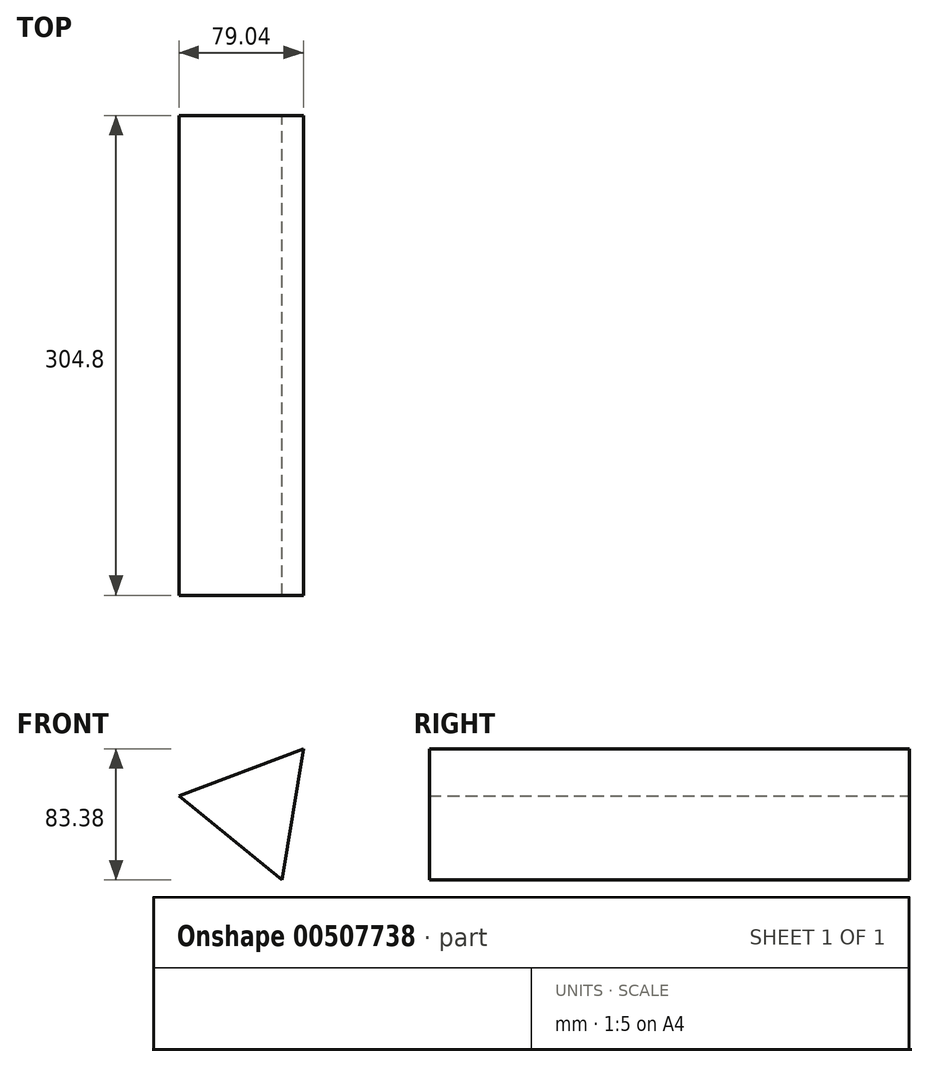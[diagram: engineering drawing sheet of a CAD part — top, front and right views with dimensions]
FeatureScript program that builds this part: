
annotation { "Feature Type Name" : "Feature", "Feature Type Description" : "" }
export const myFeature = defineFeature(function(context is Context, id is Id, definition is map)
    precondition{}
    {
        {
            var Q0;
            Q0=qCreatedBy(makeId("Front.planeOp"),FACE);
            var sketch = newSketch(context, id + "F0", { "sketchPlane" : qUnion([Q0])});
            skCircle(sketch, "E0.cCircle", {"center": v(0, 0) * mm, "radius": 48.78 * mm, "construction": true});
            skLineSegment(sketch, "E0.0", {"start": v(30.9, 37.75) * mm, "end": v(17.24, -45.63) * mm});
            skLineSegment(sketch, "E0.1", {"start": v(17.24, -45.63) * mm, "end": v(-48.14, 7.88) * mm});
            skLineSegment(sketch, "E0.2", {"start": v(-48.14, 7.88) * mm, "end": v(30.9, 37.75) * mm});
            skSolve(sketch);
        }
        {
            var Q0;
            Q0=makeQuery(id+"F0.imprint","IMPRINT",FACE,{"disambiguationData":[TD([[makeQuery(id+"F0.imprint","IMPRINT",EDGE,{"derivedFrom":sQuery(id+"F0.wireOp",EDGE,"E0.0")}),-1.0]])]});
            extrude(context, id + "F1", {"entities" : qUnion([Q0]), "depth" : 304.8 * mm});
        }
    });
